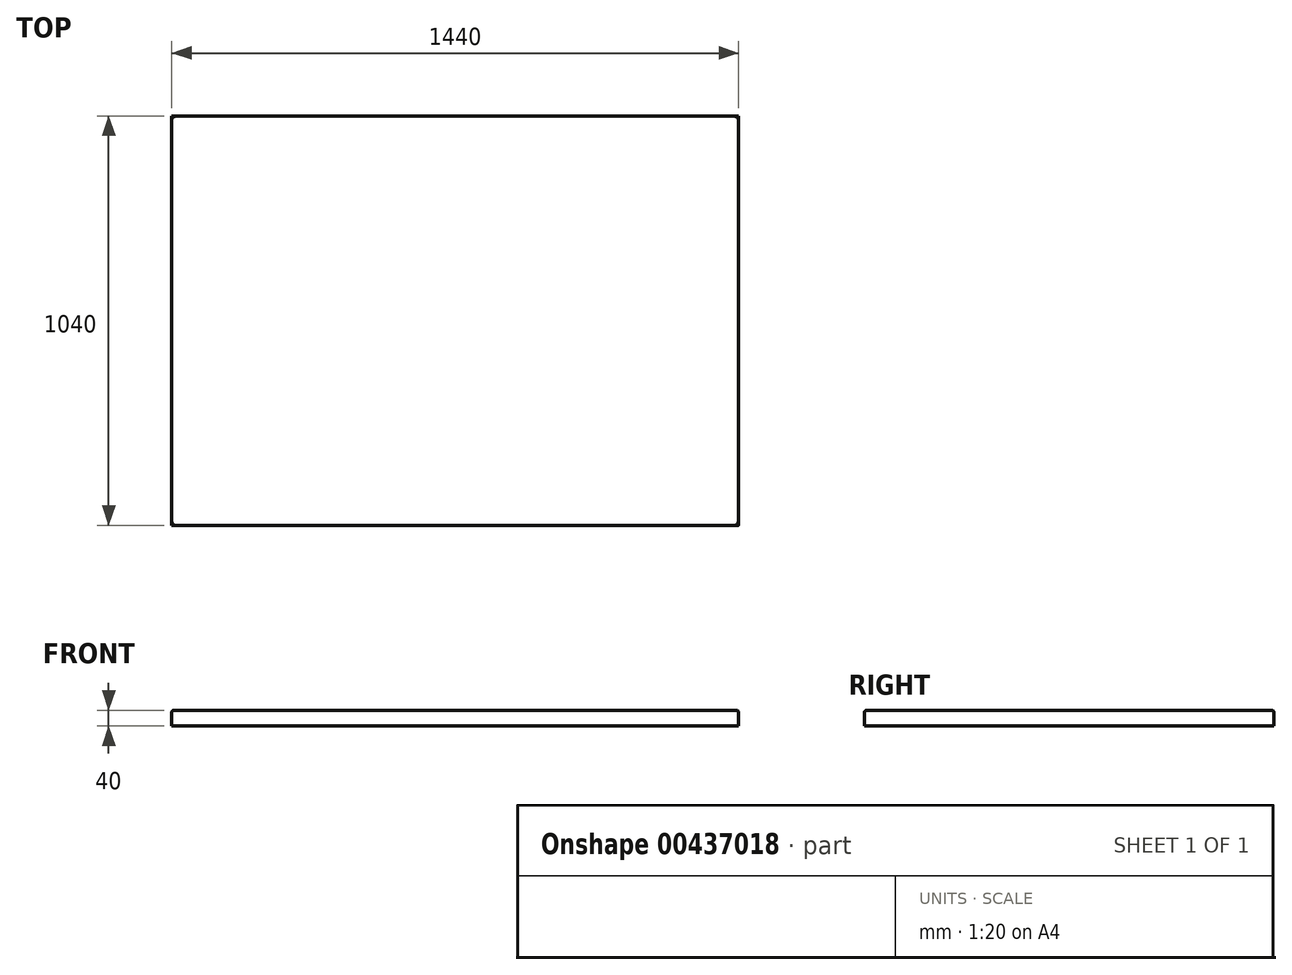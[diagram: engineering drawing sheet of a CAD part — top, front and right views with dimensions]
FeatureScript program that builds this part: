
annotation { "Feature Type Name" : "Feature", "Feature Type Description" : "" }
export const myFeature = defineFeature(function(context is Context, id is Id, definition is map)
    precondition{}
    {
        {
            var Q0;
            Q0=qCreatedBy(makeId("Right.planeOp"),FACE);
            var sketch = newSketch(context, id + "F0", { "sketchPlane" : qUnion([Q0])});
            skLineSegment(sketch, "E0.bottom", {"start": v(0, 0) * mm, "end": v(-1040, 0) * mm});
            skLineSegment(sketch, "E0.top", {"start": v(0, 40) * mm, "end": v(-1040, 40) * mm});
            skLineSegment(sketch, "E0.left", {"start": v(0, 0) * mm, "end": v(0, 40) * mm});
            skLineSegment(sketch, "E0.right", {"start": v(-1040, 0) * mm, "end": v(-1040, 40) * mm});
            skSolve(sketch);
        }
        {
            var Q0;
            Q0 = qSketchRegion(id + "F0", true);
            extrude(context, id + "F1", {"entities" : qUnion([Q0]), "depth" : 1440 * mm});
        }
        {
            var Q0;
            Q0=makeQuery(id+"F1.opExtrude","SWEPT_FACE",FACE,{"disambiguationData":[OSD([sQuery(id+"F0.wireOp",EDGE,"E0.top")])]});
            fillet(context, id + "F2", {"entities" : qUnion([Q0]), "radius" : 5 * mm, "tangentPropagation" : true, "allowEdgeOverflow" : false});
        }
    });
